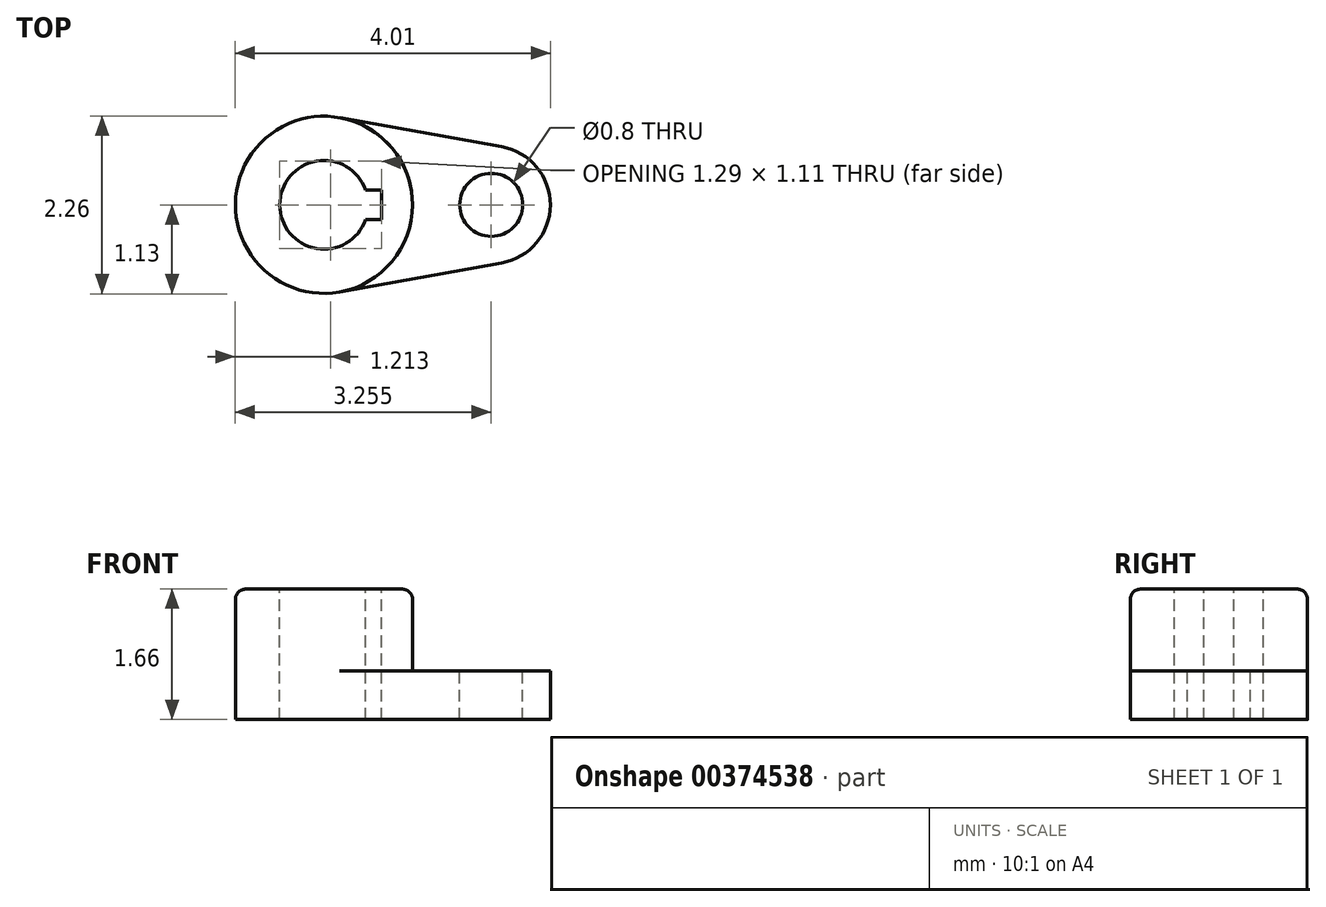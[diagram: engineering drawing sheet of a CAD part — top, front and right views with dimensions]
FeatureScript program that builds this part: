
annotation { "Feature Type Name" : "Feature", "Feature Type Description" : "" }
export const myFeature = defineFeature(function(context is Context, id is Id, definition is map)
    precondition{}
    {
        {
            var Q0;
            Q0=qCreatedBy(makeId("Top.planeOp"),FACE);
            var sketch = newSketch(context, id + "F0", { "sketchPlane" : qUnion([Q0])});
            skArc(sketch, "E0", {"start": v(0.2, 1.1) * mm, "mid": v(-1.13, 0) * mm, "end": v(0.2, -1.1) * mm});
            skArc(sketch, "E1", {"start": v(2.26, -0.74) * mm, "mid": v(2.88, 0) * mm, "end": v(2.26, 0.74) * mm});
            skLineSegment(sketch, "E2", {"start": v(0.2, 1.1) * mm, "end": v(2.26, 0.74) * mm});
            skLineSegment(sketch, "E3", {"start": v(0.2, -1.1) * mm, "end": v(2.26, -0.74) * mm});
            skSolve(sketch);
        }
        {
            var Q0;
            Q0=makeQuery(id+"F0.imprint","IMPRINT",FACE,{"disambiguationData":[TD([[makeQuery(id+"F0.imprint","IMPRINT",EDGE,{"derivedFrom":sQuery(id+"F0.wireOp",EDGE,"E0")}),1.0]])]});
            extrude(context, id + "F1", {"entities" : qUnion([Q0]), "depth" : 0.62 * mm});
        }
        {
            var Q0;
            Q0=makeQuery(id+"F1.opExtrude","CAP_FACE",FACE,{"disambiguationData":[OSD([sQuery(id+"F0.wireOp",EDGE,"E0"),sQuery(id+"F0.wireOp",EDGE,"E1"),sQuery(id+"F0.wireOp",EDGE,"E2"),sQuery(id+"F0.wireOp",EDGE,"E3")])],"isStart":false});
            var sketch = newSketch(context, id + "F2", { "sketchPlane" : qUnion([Q0])});
            skCircle(sketch, "E4", {"center": v(0, 0) * mm, "radius": 1.13 * mm});
            skSolve(sketch);
        }
        {
            var Q0;
            {var subQ0=sQuery(id+"F2.wireOp",EDGE,"E4");var subQ1=makeQuery(id+"F2.imprint","INTERSECT",VERTEX,{"derivedFrom":[makeQuery(id+"F1.opExtrude","CAP_EDGE",EDGE,{"disambiguationData":[OSD([sQuery(id+"F0.wireOp",EDGE,"E2")])],"isStart":false}),subQ0]});Q0=makeQuery(id+"F2.imprint","IMPRINT",FACE,{"disambiguationData":[TD([[makeQuery(id+"F2.imprint","IMPRINT",EDGE,{"disambiguationData":[TD([[subQ1,-1.0]])],"derivedFrom":subQ0}),1.0]])]});}
            extrude(context, id + "F3", {"entities" : qUnion([Q0]), "operationType" : NewBodyOperationType.ADD, "depth" : (1.62 - 0.58) * mm});
        }
        {
            var Q0;
            Q0=makeQuery(id+"F1.opExtrude","CAP_FACE",FACE,{"disambiguationData":[OSD([sQuery(id+"F0.wireOp",EDGE,"E0"),sQuery(id+"F0.wireOp",EDGE,"E1"),sQuery(id+"F0.wireOp",EDGE,"E2"),sQuery(id+"F0.wireOp",EDGE,"E3")])],"isStart":false});
            var sketch = newSketch(context, id + "F4", { "sketchPlane" : qUnion([Q0])});
            skCircle(sketch, "E5", {"center": v(2.12, 0) * mm, "radius": 0.4 * mm});
            skSolve(sketch);
        }
        {
            var Q0;
            Q0 = qSketchRegion(id + "F4", true);
            extrude(context, id + "F5", {"entities" : qUnion([Q0]), "operationType" : NewBodyOperationType.REMOVE, "endBound" : BoundingType.UP_TO_NEXT, "oppositeDirection" : true, "depth" : 25 * mm});
        }
        {
            var Q0;
            Q0=makeQuery(id+"F3.opExtrude","CAP_FACE",FACE,{"disambiguationData":[OSD([sQuery(id+"F2.wireOp",EDGE,"E4")])],"isStart":false});
            var sketch = newSketch(context, id + "F6", { "sketchPlane" : qUnion([Q0])});
            skArc(sketch, "E6", {"start": v(0.53, 0.2) * mm, "mid": v(-0.56, 0) * mm, "end": v(0.53, -0.2) * mm});
            skLineSegment(sketch, "E7", {"start": v(0.53, 0.19) * mm, "end": v(0.73, 0.19) * mm});
            skLineSegment(sketch, "E8", {"start": v(0.73, 0.19) * mm, "end": v(0.73, -0.19) * mm});
            skLineSegment(sketch, "E9", {"start": v(0.73, -0.19) * mm, "end": v(0.53, -0.2) * mm});
            skSolve(sketch);
        }
        {
            var Q0;
            Q0=makeQuery(id+"F6.imprint","IMPRINT",FACE,{"disambiguationData":[TD([[makeQuery(id+"F6.imprint","IMPRINT",EDGE,{"derivedFrom":sQuery(id+"F6.wireOp",EDGE,"E6")}),1.0]])]});
            extrude(context, id + "F7", {"entities" : qUnion([Q0]), "operationType" : NewBodyOperationType.REMOVE, "endBound" : BoundingType.SYMMETRIC, "oppositeDirection" : true, "depth" : 25 * mm});
        }
        {
            var Q0;
            Q0=makeQuery(id+"F3.opExtrude","CAP_EDGE",EDGE,{"disambiguationData":[OSD([sQuery(id+"F2.wireOp",EDGE,"E4")])],"isStart":false});
            fillet(context, id + "F8", {"entities" : qUnion([Q0]), "radius" : 0.13 * mm, "tangentPropagation" : true, "allowEdgeOverflow" : false});
        }
    });
